# Revit family: Heat Pump-Rheem-A2W-16kW-Vertical A
name_source: partatom
category: Mechanical Equipment
revit_build: Autodesk Revit 2016 (Build: 20190508_0715(x64)
units: mm (PartAtom-declared; Revit-internal decimal feet)

## family parameters
Always vertical = Yes
Cut with Voids When Loaded = No
OmniClass Number = 23.75.10.21
OmniClass Title = Heat Pumps
Part Type = Normal
Room Calculation Point = No
Round Connector Dimension = Use Radius
Shared = No
Work Plane-Based = No

## types (2) — shared parameters
ApparentLoad_ANZRS = 16 kW
InletPipeDiameter = 32 mm  [stored 0.104987 ft]
Length_ANZRS = 1155 mm  [stored 3.78937 ft]
Manufacturer = Rheem
Material_ANZRS = Rheem-Steel-Grey
OutletPipeDiameter = 32 mm  [stored 0.104987 ft]
PipeInsetSide = 35 mm  [stored 0.114829 ft]
PowerFactor_ANZRS = 1
SupportInsetSide = 68 mm
URL = https://www.rheem.com.au
Voltage_ANZRS = 230 V
Wattage_ANZRS = 16 kW
Width_ANZRS = 565 mm  [stored 1.85367 ft]
calcInletPipeRadius = 16 mm  [stored 0.0524934 ft]
calcOutletPipeRad = 16 mm  [stored 0.0524934 ft]

## per-type parameters (varying)
| type | Description | Height_ANZRS | Model | Show Fan Frame | calcFanGuardDepth | calcLeftFanOffset | calcRightFanOffset |
| 95301600 | Rheem's Commercial Air to Water (A2W) Heat Pump is designed with the commercial user in mind. A truly commercial grade heat pump that delivers hot water at 65°C with a system Coefficient of Performance (COP) up to 4.0. Non ducted models are generally designed for outdoor installations. Non ducted models may be installed indoors, without ducting, if a sufficient supply of heat energy is available. | 1011 mm  [stored 3.31693 ft] | Rheem Commercial Air to Water Heat Pump – 16kW Vertical Discharge & Non Ducted | No | 27 mm  [stored 0.0885827 ft] | 281 mm  [stored 0.921916 ft] | 255 mm  [stored 0.836614 ft] |
| 95201600 | Rheem's Commercial Air to Water (A2W) Heat Pump is designed with the commercial user in mind. A truly commercial grade heat pump that delivers hot water at 65°C with a system Coefficient of Performance (COP) up to 4.0. Ducted models are designed to be connected to ducting to convey cold discharge air away from the heat pump air inlet if a sufficient supply of heat energy is not available in the installation area. | 1102 mm  [stored 3.61549 ft] | Rheem Commercial Air to Water Heat Pump – 16kW Vertical Discharge & Ducted | Yes | 117 mm  [stored 0.383858 ft] | 280 mm  [stored 0.918635 ft] | 256 mm  [stored 0.839895 ft] |

note: column(s) folded — value = type name in every type: ProductCode_ANZRS

note: [stored X ft] marks values corroborated as IEEE doubles in the binary element streams (Revit-internal decimal feet)

## geometry (parser evidence)
native form markers: Blend x8, Sweep x9
no freeform markers — native parametric forms only
